# Revit family: S-24C_RAYNOR_GARAGE_DOOR
name_source: partatom
category: Doors
units: mm (PartAtom-declared; Revit-internal decimal feet)

## family parameters
Always vertical = Yes
Classification Number = 23.30.10.00
Cut with Voids When Loaded = No
Host = Wall
Room Calculation Point = No
Shared = No

## types (5) — shared parameters
Analytic Construction = <None>
Description = Sectional Ribbed Doors
Function = Exterior
Height = 0' - 0"
Manufacturer = RAYNOR
Model = S-24C
Rough Height = 0' - 0"
Rough Width = 0' - 0"
Thickness = 0' - 0"
URL = https://raynor.com
Wall Closure = By host
Width = 0' - 0"

## per-type parameters (varying)
| type | FULL VERTICAL LIFT | HIGH LIFT | LEFT MOTOR-FULL VERTICAL LIFT | LEFT MOTOR-HIGH LIFT | RIGHT MOTOR-FULL VERTICAL LIFT | RIGHT MOTOR-HIGH LIFT |
| FULL VERTICAL LIFT - LEFT MOTOR | Yes | No | Yes | No | No | No |
| FULL VERTICAL LIFT - RIGHT MOTOR | Yes | No | No | No | Yes | No |
| HIGH LIFT - LEFT MOTOR | No | Yes | No | Yes | No | No |
| HIGH LIFT - RIGHT MOTOR | No | Yes | No | No | No | Yes |
| NORMAL HEADROOM | No | No | No | No | No | No |

type visibility flags (boolean, named after types; folded from table):
- FULL VERTICAL LIFT - LEFT MOTOR: Yes: (none)
- FULL VERTICAL LIFT - RIGHT MOTOR: Yes: (none)
- HIGH LIFT - LEFT MOTOR: Yes: (none)
- HIGH LIFT - RIGHT MOTOR: Yes: (none)
- NORMAL HEADROOM: Yes: NORMAL HEADROOM

## geometry (parser evidence)
native form markers: Blend x4, Sweep x31
no freeform markers — native parametric forms only
